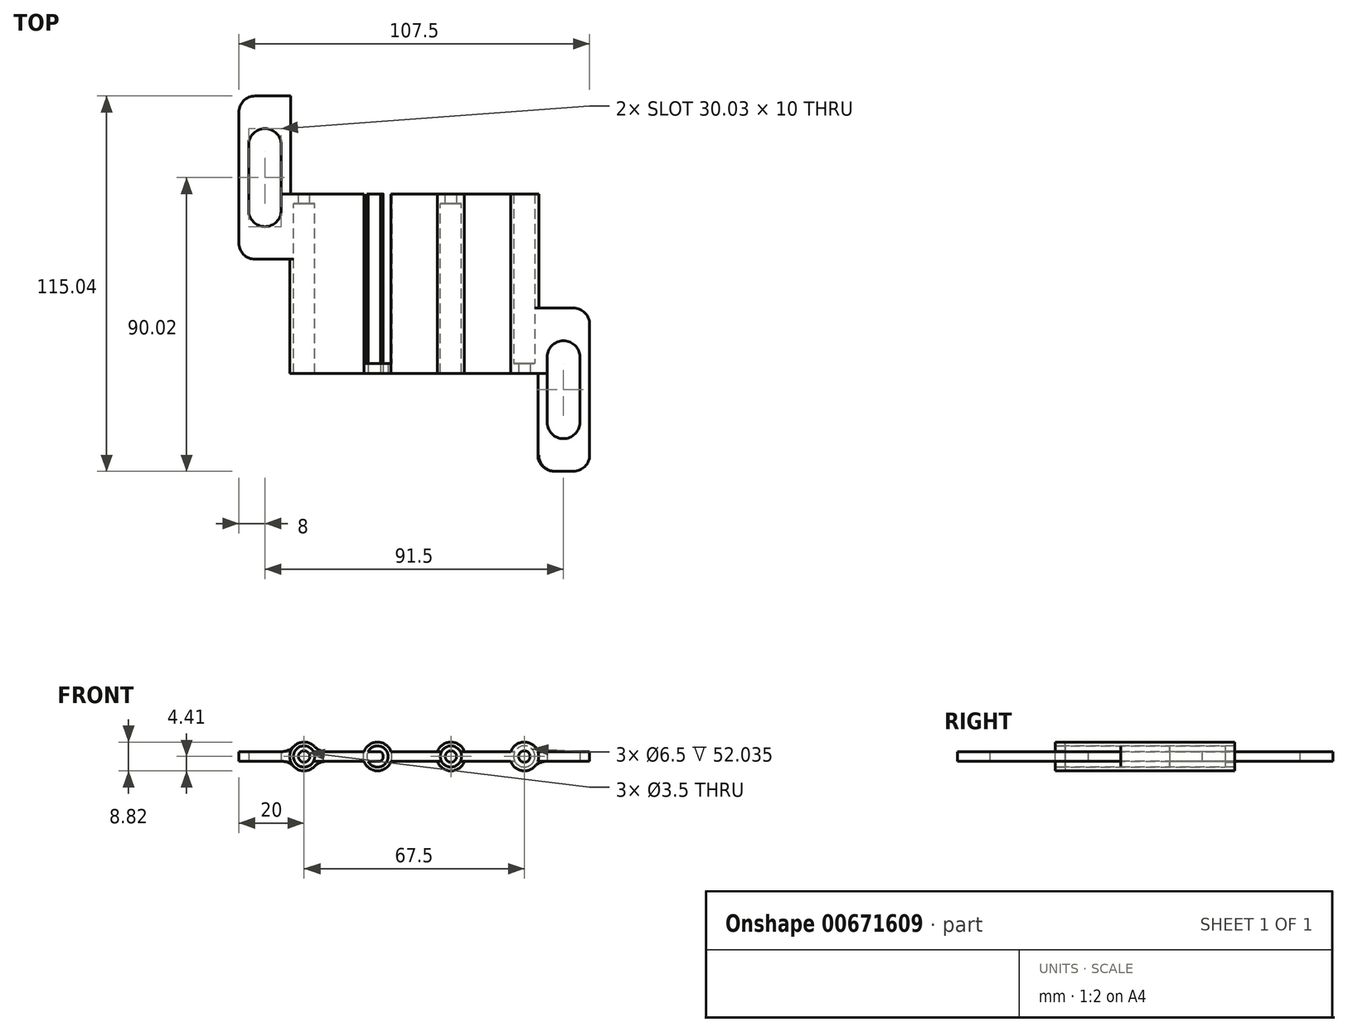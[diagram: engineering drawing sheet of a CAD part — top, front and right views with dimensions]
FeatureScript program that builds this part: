
annotation { "Feature Type Name" : "Feature", "Feature Type Description" : "" }
export const myFeature = defineFeature(function(context is Context, id is Id, definition is map)
    precondition{}
    {
        {
            var Q0;
            Q0=qCreatedBy(makeId("Top.planeOp"),FACE);
            var sketch = newSketch(context, id + "F0", { "sketchPlane" : qUnion([Q0])});
            skLineSegment(sketch, "E0.bottom", {"start": v(36.75, 27.52) * mm, "end": v(-30.75, 27.52) * mm});
            skLineSegment(sketch, "E0.top", {"start": v(36.75, -27.52) * mm, "end": v(-30.75, -27.52) * mm});
            skLineSegment(sketch, "E0.left", {"start": v(36.75, 27.52) * mm, "end": v(36.75, -27.52) * mm});
            skLineSegment(sketch, "E0.right", {"start": v(-30.75, 57.52) * mm, "end": v(-30.75, -27.52) * mm});
            skPoint(sketch, "E0.middle", {"position": v(0, 0) * mm});
            skLineSegment(sketch, "E1.left", {"start": v(36.75, 27.52) * mm, "end": v(36.75, -57.52) * mm});
            skLineSegment(sketch, "E2.0", {"start": v(56.75, -7.48) * mm, "end": v(56.75, -57.52) * mm});
            skLineSegment(sketch, "E3.0", {"start": v(-50.75, 57.52) * mm, "end": v(-50.75, 7.48) * mm});
            skLineSegment(sketch, "E4", {"start": v(36.75, -7.48) * mm, "end": v(56.75, -7.48) * mm});
            skLineSegment(sketch, "E5", {"start": v(-30.75, 7.48) * mm, "end": v(-50.75, 7.48) * mm});
            skLineSegment(sketch, "E6.0", {"start": v(-30.75, 57.52) * mm, "end": v(-50.75, 57.52) * mm});
            skLineSegment(sketch, "E7.0", {"start": v(36.75, -57.52) * mm, "end": v(56.75, -57.52) * mm});
            skLineSegment(sketch, "E8.0", {"start": v(-47.75, 47.52) * mm, "end": v(-47.75, 17.48) * mm});
            skLineSegment(sketch, "E9.0", {"start": v(-37.75, 47.52) * mm, "end": v(-37.75, 17.48) * mm});
            skLineSegment(sketch, "E10.0", {"start": v(-37.75, 47.52) * mm, "end": v(-47.75, 47.52) * mm});
            skLineSegment(sketch, "E11.0", {"start": v(-37.75, 17.48) * mm, "end": v(-47.75, 17.48) * mm});
            skLineSegment(sketch, "E12.0", {"start": v(43.75, -17.48) * mm, "end": v(53.75, -17.48) * mm});
            skLineSegment(sketch, "E13.0", {"start": v(43.75, -47.52) * mm, "end": v(53.75, -47.52) * mm});
            skLineSegment(sketch, "E14.0", {"start": v(53.75, -17.48) * mm, "end": v(53.75, -47.52) * mm});
            skLineSegment(sketch, "E15.trimOffspring", {"start": v(43.75, -17.48) * mm, "end": v(43.75, -47.52) * mm});
            skLineSegment(sketch, "E16", {"start": v(-47.75, 32.5) * mm, "end": v(23.52, 32.5) * mm, "construction": true});
            skLineSegment(sketch, "E17", {"start": v(43.75, -32.5) * mm, "end": v(9.04, -32.5) * mm, "construction": true});
            skSolve(sketch);
        }
        {
            var Q0;
            Q0=makeQuery(id+"F0.imprint","IMPRINT",FACE,{"disambiguationData":[TD([[makeQuery(id+"F0.imprint","IMPRINT",EDGE,{"derivedFrom":sQuery(id+"F0.wireOp",EDGE,"E0.bottom")}),1.0]])]});
            extrude(context, id + "F1", {"entities" : qUnion([Q0]), "depth" : 3 * mm, "offsetDistance" : 25 * mm});
        }
        {
            var Q0;
            Q0=makeQuery(id+"F1.opExtrude","SWEPT_FACE",FACE,{"disambiguationData":[OSD([sQuery(id+"F0.wireOp",EDGE,"E0.top")])]});
            var sketch = newSketch(context, id + "F2", { "sketchPlane" : qUnion([Q0])});
            skCircle(sketch, "E18", {"center": v(36.75, 1.5) * mm, "radius": 1.75 * mm});
            skCircle(sketch, "E19", {"center": v(36.75, 1.5) * mm, "radius": 3.25 * mm});
            skCircle(sketch, "E20", {"center": v(36.75, 1.5) * mm, "radius": 4.4 * mm});
            skLineSegment(sketch, "E21", {"start": v(36.75, 1.5) * mm, "end": v(36.75, 12.8) * mm, "construction": true});
            skLineSegment(sketch, "E22.0", {"start": v(-8.25, 1.5) * mm, "end": v(-8.25, 12.8) * mm, "construction": true});
            skLineSegment(sketch, "E23", {"start": v(-8.25, 12.8) * mm, "end": v(36.75, 12.8) * mm, "construction": true});
            skLineSegment(sketch, "E24", {"start": v(14.25, 12.8) * mm, "end": v(14.25, 1.5) * mm, "construction": true});
            skCircle(sketch, "E25.MirrorC", {"center": v(-8.25, 1.5) * mm, "radius": 4.4 * mm});
            skCircle(sketch, "E26.MirrorC", {"center": v(-8.25, 1.5) * mm, "radius": 3.25 * mm});
            skCircle(sketch, "E27.MirrorC", {"center": v(-8.25, 1.5) * mm, "radius": 1.75 * mm});
            skSolve(sketch);
        }
        {
            var Q0;
            Q0 = qSketchRegion(id + "F2", true);
            extrude(context, id + "F3", {"entities" : qUnion([Q0]), "operationType" : NewBodyOperationType.ADD, "oppositeDirection" : true, "depth" : 55 * mm, "offsetDistance" : 25 * mm});
        }
        {
            var Q0;
            {var subQ0=sQuery(id+"F2.wireOp",EDGE,"E18");var subQ1=sQuery(id+"F0.wireOp",EDGE,"E0.top");var subQ2=makeQuery(id+"F1.opExtrude","CAP_EDGE",EDGE,{"disambiguationData":[OSD([subQ1])],"isStart":true});var subQ3=makeQuery(id+"F2.imprint","INTERSECT",VERTEX,{"derivedFrom":[subQ2,subQ0]});Q0=makeQuery(id+"F2.imprint","IMPRINT",FACE,{"disambiguationData":[TD([[makeQuery(id+"F2.imprint","IMPRINT",EDGE,{"disambiguationData":[TD([[subQ3,-1.0]])],"derivedFrom":subQ0}),-1.0]])]});}
            var Q1;
            {var subQ0=sQuery(id+"F2.wireOp",EDGE,"E26.MirrorC");var subQ1=makeQuery(id+"F1.opExtrude","CAP_EDGE",EDGE,{"disambiguationData":[OSD([sQuery(id+"F0.wireOp",EDGE,"E0.top")])],"isStart":true});var subQ2=makeQuery(id+"F2.imprint","INTERSECT",VERTEX,{"disambiguationData":[OD(0.0)],"derivedFrom":[subQ1,subQ0]});Q1=makeQuery(id+"F2.imprint","IMPRINT",FACE,{"disambiguationData":[TD([[makeQuery(id+"F2.imprint","IMPRINT",EDGE,{"disambiguationData":[TD([[subQ2,1.0]])],"derivedFrom":subQ0}),-1.0]])]});}
            var Q2;
            {var subQ0=sQuery(id+"F2.wireOp",EDGE,"E26.MirrorC");var subQ1=makeQuery(id+"F1.opExtrude","CAP_EDGE",EDGE,{"disambiguationData":[OSD([sQuery(id+"F0.wireOp",EDGE,"E0.top")])],"isStart":false});var subQ2=makeQuery(id+"F2.imprint","INTERSECT",VERTEX,{"disambiguationData":[OD(0.0)],"derivedFrom":[subQ1,subQ0]});Q2=makeQuery(id+"F2.imprint","IMPRINT",FACE,{"disambiguationData":[TD([[makeQuery(id+"F2.imprint","IMPRINT",EDGE,{"disambiguationData":[TD([[subQ2,-1.0]])],"derivedFrom":subQ0}),-1.0]])]});}
            var Q3;
            {var subQ1=sQuery(id+"F0.wireOp",EDGE,"E0.top");var subQ6=makeQuery(id+"F1.opExtrude","SWEPT_EDGE",EDGE,{"disambiguationData":[OSD([subQ1,sQuery(id+"F0.wireOp",EDGE,"E0.left")])]});Q3=makeQuery(id+"F2.imprint","IMPRINT",FACE,{"disambiguationData":[TD([[makeQuery(id+"F2.imprint","IMPRINT",EDGE,{"derivedFrom":subQ6}),-1.0]])]});}
            var Q4;
            {var subQ0=sQuery(id+"F2.wireOp",EDGE,"E18");var subQ1=sQuery(id+"F0.wireOp",EDGE,"E0.top");var subQ2=makeQuery(id+"F1.opExtrude","CAP_EDGE",EDGE,{"disambiguationData":[OSD([subQ1])],"isStart":true});var subQ3=makeQuery(id+"F2.imprint","INTERSECT",VERTEX,{"derivedFrom":[subQ2,subQ0]});Q4=makeQuery(id+"F2.imprint","IMPRINT",FACE,{"disambiguationData":[TD([[makeQuery(id+"F2.imprint","IMPRINT",EDGE,{"disambiguationData":[TD([[subQ3,1.0]])],"derivedFrom":subQ0}),-1.0]])]});}
            var Q5;
            {var subQ0=sQuery(id+"F2.wireOp",EDGE,"E26.MirrorC");var subQ1=sQuery(id+"F0.wireOp",EDGE,"E0.top");var subQ2=makeQuery(id+"F1.opExtrude","CAP_EDGE",EDGE,{"disambiguationData":[OSD([subQ1])],"isStart":false});var subQ3=makeQuery(id+"F2.imprint","INTERSECT",VERTEX,{"disambiguationData":[OD(0.0)],"derivedFrom":[subQ2,subQ0]});Q5=makeQuery(id+"F2.imprint","IMPRINT",FACE,{"disambiguationData":[TD([[makeQuery(id+"F2.imprint","IMPRINT",EDGE,{"disambiguationData":[TD([[subQ3,1.0]])],"derivedFrom":subQ0}),-1.0]])]});}
            var Q6;
            {var subQ0=sQuery(id+"F2.wireOp",EDGE,"E27.MirrorC");var subQ1=sQuery(id+"F0.wireOp",EDGE,"E0.top");var subQ2=makeQuery(id+"F1.opExtrude","CAP_EDGE",EDGE,{"disambiguationData":[OSD([subQ1])],"isStart":false});var subQ3=makeQuery(id+"F2.imprint","INTERSECT",VERTEX,{"disambiguationData":[OD(0.0)],"derivedFrom":[subQ2,subQ0]});Q6=makeQuery(id+"F2.imprint","IMPRINT",FACE,{"disambiguationData":[TD([[makeQuery(id+"F2.imprint","IMPRINT",EDGE,{"disambiguationData":[TD([[subQ3,1.0]])],"derivedFrom":subQ0}),-1.0]])]});}
            var Q7;
            {var subQ0=sQuery(id+"F2.wireOp",EDGE,"E26.MirrorC");var subQ1=sQuery(id+"F0.wireOp",EDGE,"E0.top");var subQ2=makeQuery(id+"F1.opExtrude","CAP_EDGE",EDGE,{"disambiguationData":[OSD([subQ1])],"isStart":false});var subQ3=makeQuery(id+"F2.imprint","INTERSECT",VERTEX,{"disambiguationData":[OD(1.0)],"derivedFrom":[subQ2,subQ0]});Q7=makeQuery(id+"F2.imprint","IMPRINT",FACE,{"disambiguationData":[TD([[makeQuery(id+"F2.imprint","IMPRINT",EDGE,{"disambiguationData":[TD([[subQ3,-1.0]])],"derivedFrom":subQ0}),-1.0]])]});}
            extrude(context, id + "F4", {"entities" : qUnion([Q0, Q1, Q2, Q3, Q4, Q5, Q6, Q7]), "operationType" : NewBodyOperationType.REMOVE, "oppositeDirection" : true, "depth" : 60 * mm, "offsetDistance" : 25 * mm});
        }
        {
            var Q0;
            {var subQ0=sQuery(id+"F2.wireOp",EDGE,"E26.MirrorC");var subQ1=makeQuery(id+"F1.opExtrude","CAP_EDGE",EDGE,{"disambiguationData":[OSD([sQuery(id+"F0.wireOp",EDGE,"E0.top")])],"isStart":false});var subQ2=makeQuery(id+"F2.imprint","INTERSECT",VERTEX,{"disambiguationData":[OD(0.0)],"derivedFrom":[subQ1,subQ0]});Q0=makeQuery(id+"F2.imprint","IMPRINT",FACE,{"disambiguationData":[TD([[makeQuery(id+"F2.imprint","IMPRINT",EDGE,{"disambiguationData":[TD([[subQ2,-1.0]])],"derivedFrom":subQ0}),-1.0]])]});}
            var Q1;
            {var subQ0=sQuery(id+"F2.wireOp",EDGE,"E26.MirrorC");var subQ1=sQuery(id+"F0.wireOp",EDGE,"E0.top");var subQ2=makeQuery(id+"F1.opExtrude","CAP_EDGE",EDGE,{"disambiguationData":[OSD([subQ1])],"isStart":false});var subQ3=makeQuery(id+"F2.imprint","INTERSECT",VERTEX,{"disambiguationData":[OD(0.0)],"derivedFrom":[subQ2,subQ0]});Q1=makeQuery(id+"F2.imprint","IMPRINT",FACE,{"disambiguationData":[TD([[makeQuery(id+"F2.imprint","IMPRINT",EDGE,{"disambiguationData":[TD([[subQ3,1.0]])],"derivedFrom":subQ0}),-1.0]])]});}
            var Q2;
            {var subQ0=sQuery(id+"F2.wireOp",EDGE,"E26.MirrorC");var subQ1=makeQuery(id+"F1.opExtrude","CAP_EDGE",EDGE,{"disambiguationData":[OSD([sQuery(id+"F0.wireOp",EDGE,"E0.top")])],"isStart":true});var subQ2=makeQuery(id+"F2.imprint","INTERSECT",VERTEX,{"disambiguationData":[OD(0.0)],"derivedFrom":[subQ1,subQ0]});Q2=makeQuery(id+"F2.imprint","IMPRINT",FACE,{"disambiguationData":[TD([[makeQuery(id+"F2.imprint","IMPRINT",EDGE,{"disambiguationData":[TD([[subQ2,1.0]])],"derivedFrom":subQ0}),-1.0]])]});}
            var Q3;
            {var subQ0=sQuery(id+"F2.wireOp",EDGE,"E26.MirrorC");var subQ1=sQuery(id+"F0.wireOp",EDGE,"E0.top");var subQ2=makeQuery(id+"F1.opExtrude","CAP_EDGE",EDGE,{"disambiguationData":[OSD([subQ1])],"isStart":false});var subQ3=makeQuery(id+"F2.imprint","INTERSECT",VERTEX,{"disambiguationData":[OD(1.0)],"derivedFrom":[subQ2,subQ0]});Q3=makeQuery(id+"F2.imprint","IMPRINT",FACE,{"disambiguationData":[TD([[makeQuery(id+"F2.imprint","IMPRINT",EDGE,{"disambiguationData":[TD([[subQ3,-1.0]])],"derivedFrom":subQ0}),-1.0]])]});}
            var Q4;
            {var subQ0=sQuery(id+"F2.wireOp",EDGE,"E18");var subQ1=sQuery(id+"F0.wireOp",EDGE,"E0.top");var subQ2=makeQuery(id+"F1.opExtrude","CAP_EDGE",EDGE,{"disambiguationData":[OSD([subQ1])],"isStart":true});var subQ3=makeQuery(id+"F2.imprint","INTERSECT",VERTEX,{"derivedFrom":[subQ2,subQ0]});Q4=makeQuery(id+"F2.imprint","IMPRINT",FACE,{"disambiguationData":[TD([[makeQuery(id+"F2.imprint","IMPRINT",EDGE,{"disambiguationData":[TD([[subQ3,1.0]])],"derivedFrom":subQ0}),-1.0]])]});}
            var Q5;
            {var subQ0=sQuery(id+"F2.wireOp",EDGE,"E18");var subQ1=sQuery(id+"F0.wireOp",EDGE,"E0.top");var subQ2=makeQuery(id+"F1.opExtrude","CAP_EDGE",EDGE,{"disambiguationData":[OSD([subQ1])],"isStart":true});var subQ3=makeQuery(id+"F2.imprint","INTERSECT",VERTEX,{"derivedFrom":[subQ2,subQ0]});Q5=makeQuery(id+"F2.imprint","IMPRINT",FACE,{"disambiguationData":[TD([[makeQuery(id+"F2.imprint","IMPRINT",EDGE,{"disambiguationData":[TD([[subQ3,-1.0]])],"derivedFrom":subQ0}),-1.0]])]});}
            extrude(context, id + "F5", {"entities" : qUnion([Q0, Q1, Q2, Q3, Q4, Q5]), "operationType" : NewBodyOperationType.ADD, "oppositeDirection" : true, "depth" : 3 * mm, "offsetDistance" : 25 * mm});
        }
        {
            var Q0;
            {var subQ1=sQuery(id+"F2.wireOp",EDGE,"E19");var subQ5=sQuery(id+"F0.wireOp",EDGE,"E0.bottom");Q0=makeQuery(id+"F4.boolean.opBoolean","SPLIT",FACE,{"disambiguationData":[TD([makeQuery(id+"F3.opExtrude","SWEPT_FACE",FACE,{"disambiguationData":[OSD([subQ1])]})])],"derivedFrom":makeQuery(id+"F1.opExtrude","SWEPT_FACE",FACE,{"disambiguationData":[OSD([subQ5])]})});}
            var sketch = newSketch(context, id + "F6", { "sketchPlane" : qUnion([Q0])});
            skLineSegment(sketch, "E28", {"start": v(-14.25, 3) * mm, "end": v(-14.25, 0) * mm, "construction": true});
            skCircle(sketch, "E29", {"center": v(-14.25, 1.5) * mm, "radius": 1.75 * mm});
            skCircle(sketch, "E30", {"center": v(-14.25, 1.5) * mm, "radius": 3.25 * mm});
            skCircle(sketch, "E31", {"center": v(-14.25, 1.5) * mm, "radius": 4.4 * mm});
            skCircle(sketch, "E32.1.0.0", {"center": v(30.75, 1.5) * mm, "radius": 4.4 * mm});
            skCircle(sketch, "E32.1.0.1", {"center": v(30.75, 1.5) * mm, "radius": 3.25 * mm});
            skCircle(sketch, "E32.1.0.2", {"center": v(30.75, 1.5) * mm, "radius": 1.75 * mm});
            skLineSegment(sketch, "E32.direction1", {"start": v(-14.25, 1.5) * mm, "end": v(30.75, 1.5) * mm, "construction": true});
            skSolve(sketch);
        }
        {
            var Q0;
            Q0=makeQuery(id+"F0.imprint","IMPRINT",FACE,{"disambiguationData":[TD([[makeQuery(id+"F0.imprint","IMPRINT",EDGE,{"derivedFrom":sQuery(id+"F0.wireOp",EDGE,"E0.right")}),-1.0]])]});
            var Q1;
            {var subQ1=sQuery(id+"F0.wireOp",EDGE,"E1.left");Q1=makeQuery(id+"F0.imprint","IMPRINT",FACE,{"disambiguationData":[TD([[makeQuery(id+"F0.imprint","IMPRINT",EDGE,{"derivedFrom":subQ1}),1.0]])]});}
            extrude(context, id + "F7", {"entities" : qUnion([Q0, Q1]), "operationType" : NewBodyOperationType.ADD, "depth" : 3 * mm, "offsetDistance" : 25 * mm});
        }
        {
            var Q0;
            {var subQ0=sQuery(id+"F6.wireOp",EDGE,"E30");var subQ1=sQuery(id+"F2.wireOp",EDGE,"E19");var subQ2=sQuery(id+"F0.wireOp",EDGE,"E0.bottom");var subQ4=makeQuery(id+"F4.boolean.opBoolean","SPLIT",EDGE,{"disambiguationData":[TD([makeQuery(id+"F3.opExtrude","SWEPT_FACE",FACE,{"disambiguationData":[OSD([subQ1])]})])],"derivedFrom":makeQuery(id+"F1.opExtrude","CAP_EDGE",EDGE,{"disambiguationData":[OSD([subQ2])],"isStart":false})});var subQ5=makeQuery(id+"F6.imprint","INTERSECT",VERTEX,{"disambiguationData":[OD(0.0)],"derivedFrom":[subQ4,subQ0]});Q0=makeQuery(id+"F6.imprint","IMPRINT",FACE,{"disambiguationData":[TD([[makeQuery(id+"F6.imprint","IMPRINT",EDGE,{"disambiguationData":[TD([[subQ5,1.0]])],"derivedFrom":subQ0}),-1.0]])]});}
            var Q1;
            {var subQ0=sQuery(id+"F6.wireOp",EDGE,"E30");var subQ1=sQuery(id+"F2.wireOp",EDGE,"E19");var subQ2=sQuery(id+"F0.wireOp",EDGE,"E0.bottom");var subQ4=makeQuery(id+"F4.boolean.opBoolean","SPLIT",EDGE,{"disambiguationData":[TD([makeQuery(id+"F3.opExtrude","SWEPT_FACE",FACE,{"disambiguationData":[OSD([subQ1])]})])],"derivedFrom":makeQuery(id+"F1.opExtrude","CAP_EDGE",EDGE,{"disambiguationData":[OSD([subQ2])],"isStart":true})});var subQ5=makeQuery(id+"F6.imprint","INTERSECT",VERTEX,{"disambiguationData":[OD(0.0)],"derivedFrom":[subQ4,subQ0]});Q1=makeQuery(id+"F6.imprint","IMPRINT",FACE,{"disambiguationData":[TD([[makeQuery(id+"F6.imprint","IMPRINT",EDGE,{"disambiguationData":[TD([[subQ5,-1.0]])],"derivedFrom":subQ0}),-1.0]])]});}
            var Q2;
            Q2=makeQuery(id+"F6.imprint","IMPRINT",FACE,{"disambiguationData":[TD([[makeQuery(id+"F6.imprint","IMPRINT",EDGE,{"derivedFrom":sQuery(id+"F6.wireOp",EDGE,"E32.1.0.0")}),1.0]])]});
            extrude(context, id + "F8", {"entities" : qUnion([Q0, Q1, Q2]), "operationType" : NewBodyOperationType.ADD, "oppositeDirection" : true, "depth" : 55 * mm, "offsetDistance" : 25 * mm});
        }
        {
            var Q0;
            {var subQ0=sQuery(id+"F6.wireOp",EDGE,"E29");var subQ1=sQuery(id+"F2.wireOp",EDGE,"E19");var subQ2=makeQuery(id+"F3.opExtrude","SWEPT_FACE",FACE,{"disambiguationData":[OSD([subQ1])]});var subQ6=sQuery(id+"F0.wireOp",EDGE,"E0.bottom");var subQ12=makeQuery(id+"F4.boolean.opBoolean","SPLIT",EDGE,{"disambiguationData":[TD([subQ2])],"derivedFrom":makeQuery(id+"F1.opExtrude","CAP_EDGE",EDGE,{"disambiguationData":[OSD([subQ6])],"isStart":true})});var subQ13=makeQuery(id+"F6.imprint","INTERSECT",VERTEX,{"disambiguationData":[OD(0.0)],"derivedFrom":[subQ12,subQ0]});Q0=makeQuery(id+"F6.imprint","IMPRINT",FACE,{"disambiguationData":[TD([[makeQuery(id+"F6.imprint","IMPRINT",EDGE,{"disambiguationData":[TD([[subQ13,1.0]])],"derivedFrom":subQ0}),-1.0]])]});}
            var Q1;
            {var subQ0=sQuery(id+"F6.wireOp",EDGE,"E29");var subQ1=sQuery(id+"F2.wireOp",EDGE,"E19");var subQ2=makeQuery(id+"F3.opExtrude","SWEPT_FACE",FACE,{"disambiguationData":[OSD([subQ1])]});var subQ6=sQuery(id+"F0.wireOp",EDGE,"E0.bottom");var subQ12=makeQuery(id+"F4.boolean.opBoolean","SPLIT",EDGE,{"disambiguationData":[TD([subQ2])],"derivedFrom":makeQuery(id+"F1.opExtrude","CAP_EDGE",EDGE,{"disambiguationData":[OSD([subQ6])],"isStart":true})});var subQ13=makeQuery(id+"F6.imprint","INTERSECT",VERTEX,{"disambiguationData":[OD(0.0)],"derivedFrom":[subQ12,subQ0]});Q1=makeQuery(id+"F6.imprint","IMPRINT",FACE,{"disambiguationData":[TD([[makeQuery(id+"F6.imprint","IMPRINT",EDGE,{"disambiguationData":[TD([[subQ13,1.0]])],"derivedFrom":subQ0}),1.0]])]});}
            var Q2;
            {var subQ0=sQuery(id+"F6.wireOp",EDGE,"E29");var subQ1=sQuery(id+"F2.wireOp",EDGE,"E19");var subQ2=makeQuery(id+"F3.opExtrude","SWEPT_FACE",FACE,{"disambiguationData":[OSD([subQ1])]});var subQ6=sQuery(id+"F0.wireOp",EDGE,"E0.bottom");var subQ12=makeQuery(id+"F4.boolean.opBoolean","SPLIT",EDGE,{"disambiguationData":[TD([subQ2])],"derivedFrom":makeQuery(id+"F1.opExtrude","CAP_EDGE",EDGE,{"disambiguationData":[OSD([subQ6])],"isStart":true})});var subQ13=makeQuery(id+"F6.imprint","INTERSECT",VERTEX,{"disambiguationData":[OD(1.0)],"derivedFrom":[subQ12,subQ0]});Q2=makeQuery(id+"F6.imprint","IMPRINT",FACE,{"disambiguationData":[TD([[makeQuery(id+"F6.imprint","IMPRINT",EDGE,{"disambiguationData":[TD([[subQ13,-1.0]])],"derivedFrom":subQ0}),-1.0]])]});}
            var Q3;
            Q3=makeQuery(id+"F6.imprint","IMPRINT",FACE,{"disambiguationData":[TD([[makeQuery(id+"F6.imprint","IMPRINT",EDGE,{"derivedFrom":sQuery(id+"F6.wireOp",EDGE,"E32.1.0.2")}),1.0]])]});
            var Q4;
            Q4=makeQuery(id+"F6.imprint","IMPRINT",FACE,{"disambiguationData":[TD([[makeQuery(id+"F6.imprint","IMPRINT",EDGE,{"derivedFrom":sQuery(id+"F6.wireOp",EDGE,"E32.1.0.1")}),1.0]])]});
            extrude(context, id + "F9", {"entities" : qUnion([Q0, Q1, Q2, Q3, Q4]), "operationType" : NewBodyOperationType.REMOVE, "oppositeDirection" : true, "depth" : 60 * mm, "offsetDistance" : 25 * mm});
        }
        {
            var Q0;
            {var subQ0=sQuery(id+"F6.wireOp",EDGE,"E29");var subQ1=sQuery(id+"F2.wireOp",EDGE,"E19");var subQ2=sQuery(id+"F0.wireOp",EDGE,"E0.bottom");var subQ4=makeQuery(id+"F4.boolean.opBoolean","SPLIT",EDGE,{"disambiguationData":[TD([makeQuery(id+"F3.opExtrude","SWEPT_FACE",FACE,{"disambiguationData":[OSD([subQ1])]})])],"derivedFrom":makeQuery(id+"F1.opExtrude","CAP_EDGE",EDGE,{"disambiguationData":[OSD([subQ2])],"isStart":false})});var subQ5=makeQuery(id+"F6.imprint","INTERSECT",VERTEX,{"disambiguationData":[OD(0.0)],"derivedFrom":[subQ4,subQ0]});Q0=makeQuery(id+"F6.imprint","IMPRINT",FACE,{"disambiguationData":[TD([[makeQuery(id+"F6.imprint","IMPRINT",EDGE,{"disambiguationData":[TD([[subQ5,1.0]])],"derivedFrom":subQ0}),-1.0]])]});}
            var Q1;
            {var subQ0=sQuery(id+"F6.wireOp",EDGE,"E29");var subQ1=sQuery(id+"F2.wireOp",EDGE,"E19");var subQ2=makeQuery(id+"F3.opExtrude","SWEPT_FACE",FACE,{"disambiguationData":[OSD([subQ1])]});var subQ6=sQuery(id+"F0.wireOp",EDGE,"E0.bottom");var subQ12=makeQuery(id+"F4.boolean.opBoolean","SPLIT",EDGE,{"disambiguationData":[TD([subQ2])],"derivedFrom":makeQuery(id+"F1.opExtrude","CAP_EDGE",EDGE,{"disambiguationData":[OSD([subQ6])],"isStart":true})});var subQ13=makeQuery(id+"F6.imprint","INTERSECT",VERTEX,{"disambiguationData":[OD(1.0)],"derivedFrom":[subQ12,subQ0]});Q1=makeQuery(id+"F6.imprint","IMPRINT",FACE,{"disambiguationData":[TD([[makeQuery(id+"F6.imprint","IMPRINT",EDGE,{"disambiguationData":[TD([[subQ13,-1.0]])],"derivedFrom":subQ0}),-1.0]])]});}
            var Q2;
            {var subQ0=sQuery(id+"F6.wireOp",EDGE,"E29");var subQ1=sQuery(id+"F2.wireOp",EDGE,"E19");var subQ2=sQuery(id+"F0.wireOp",EDGE,"E0.bottom");var subQ4=makeQuery(id+"F4.boolean.opBoolean","SPLIT",EDGE,{"disambiguationData":[TD([makeQuery(id+"F3.opExtrude","SWEPT_FACE",FACE,{"disambiguationData":[OSD([subQ1])]})])],"derivedFrom":makeQuery(id+"F1.opExtrude","CAP_EDGE",EDGE,{"disambiguationData":[OSD([subQ2])],"isStart":true})});var subQ5=makeQuery(id+"F6.imprint","INTERSECT",VERTEX,{"disambiguationData":[OD(0.0)],"derivedFrom":[subQ4,subQ0]});Q2=makeQuery(id+"F6.imprint","IMPRINT",FACE,{"disambiguationData":[TD([[makeQuery(id+"F6.imprint","IMPRINT",EDGE,{"disambiguationData":[TD([[subQ5,-1.0]])],"derivedFrom":subQ0}),-1.0]])]});}
            var Q3;
            {var subQ0=sQuery(id+"F6.wireOp",EDGE,"E29");var subQ1=sQuery(id+"F2.wireOp",EDGE,"E19");var subQ2=makeQuery(id+"F3.opExtrude","SWEPT_FACE",FACE,{"disambiguationData":[OSD([subQ1])]});var subQ6=sQuery(id+"F0.wireOp",EDGE,"E0.bottom");var subQ12=makeQuery(id+"F4.boolean.opBoolean","SPLIT",EDGE,{"disambiguationData":[TD([subQ2])],"derivedFrom":makeQuery(id+"F1.opExtrude","CAP_EDGE",EDGE,{"disambiguationData":[OSD([subQ6])],"isStart":true})});var subQ13=makeQuery(id+"F6.imprint","INTERSECT",VERTEX,{"disambiguationData":[OD(0.0)],"derivedFrom":[subQ12,subQ0]});Q3=makeQuery(id+"F6.imprint","IMPRINT",FACE,{"disambiguationData":[TD([[makeQuery(id+"F6.imprint","IMPRINT",EDGE,{"disambiguationData":[TD([[subQ13,1.0]])],"derivedFrom":subQ0}),-1.0]])]});}
            var Q4;
            Q4=makeQuery(id+"F6.imprint","IMPRINT",FACE,{"disambiguationData":[TD([[makeQuery(id+"F6.imprint","IMPRINT",EDGE,{"derivedFrom":sQuery(id+"F6.wireOp",EDGE,"E32.1.0.1")}),1.0]])]});
            extrude(context, id + "F10", {"entities" : qUnion([Q0, Q1, Q2, Q3, Q4]), "operationType" : NewBodyOperationType.ADD, "oppositeDirection" : true, "depth" : 3 * mm, "offsetDistance" : 25 * mm});
        }
        {
            var Q0;
            {var subQ0=sQuery(id+"F2.wireOp",EDGE,"E18");var subQ1=sQuery(id+"F0.wireOp",EDGE,"E0.top");var subQ2=makeQuery(id+"F1.opExtrude","CAP_EDGE",EDGE,{"disambiguationData":[OSD([subQ1])],"isStart":true});var subQ3=makeQuery(id+"F2.imprint","INTERSECT",VERTEX,{"derivedFrom":[subQ2,subQ0]});Q0=makeQuery(id+"F2.imprint","IMPRINT",FACE,{"disambiguationData":[TD([[makeQuery(id+"F2.imprint","IMPRINT",EDGE,{"disambiguationData":[TD([[subQ3,-1.0]])],"derivedFrom":subQ0}),-1.0]])]});}
            var Q1;
            {var subQ1=sQuery(id+"F0.wireOp",EDGE,"E0.top");var subQ6=makeQuery(id+"F1.opExtrude","SWEPT_EDGE",EDGE,{"disambiguationData":[OSD([subQ1,sQuery(id+"F0.wireOp",EDGE,"E0.left"),sQuery(id+"F0.wireOp",EDGE,"SqTT4nLf-HDbF-SFdv-T9V0-0vRYkoL7qoO4")])]});Q1=makeQuery(id+"F2.imprint","IMPRINT",FACE,{"disambiguationData":[TD([[makeQuery(id+"F2.imprint","IMPRINT",EDGE,{"derivedFrom":subQ6}),1.0]])]});}
            extrude(context, id + "F11", {"entities" : qUnion([Q0, Q1]), "operationType" : NewBodyOperationType.REMOVE, "oppositeDirection" : true, "depth" : 60 * mm, "offsetDistance" : 25 * mm});
        }
        {
            var Q0;
            {var subQ0=sQuery(id+"F2.wireOp",EDGE,"E18");var subQ1=sQuery(id+"F0.wireOp",EDGE,"E0.top");var subQ2=makeQuery(id+"F1.opExtrude","CAP_EDGE",EDGE,{"disambiguationData":[OSD([subQ1])],"isStart":true});var subQ3=makeQuery(id+"F2.imprint","INTERSECT",VERTEX,{"derivedFrom":[subQ2,subQ0]});Q0=makeQuery(id+"F2.imprint","IMPRINT",FACE,{"disambiguationData":[TD([[makeQuery(id+"F2.imprint","IMPRINT",EDGE,{"disambiguationData":[TD([[subQ3,-1.0]])],"derivedFrom":subQ0}),-1.0]])]});}
            extrude(context, id + "F12", {"entities" : qUnion([Q0]), "operationType" : NewBodyOperationType.ADD, "oppositeDirection" : true, "depth" : 3 * mm, "offsetDistance" : 25 * mm});
        }
        {
            var Q0;
            {var subQ0=sQuery(id+"F2.wireOp",EDGE,"E18");var subQ1=sQuery(id+"F0.wireOp",EDGE,"E0.top");var subQ2=makeQuery(id+"F1.opExtrude","CAP_EDGE",EDGE,{"disambiguationData":[OSD([subQ1])],"isStart":true});var subQ3=makeQuery(id+"F2.imprint","INTERSECT",VERTEX,{"derivedFrom":[subQ2,subQ0]});Q0=makeQuery(id+"F2.imprint","IMPRINT",FACE,{"disambiguationData":[TD([[makeQuery(id+"F2.imprint","IMPRINT",EDGE,{"disambiguationData":[TD([[subQ3,-1.0]])],"derivedFrom":subQ0}),-1.0]])]});}
            var Q1;
            Q1=makeQuery(id+"F7.opExtrude","SWEPT_FACE",FACE,{"disambiguationData":[OSD([sQuery(id+"F0.wireOp",EDGE,"E7.0")])]});
            var Q2;
            {var subQ1=sQuery(id+"F0.wireOp",EDGE,"E0.top");var subQ6=makeQuery(id+"F1.opExtrude","SWEPT_EDGE",EDGE,{"disambiguationData":[OSD([subQ1,sQuery(id+"F0.wireOp",EDGE,"E0.left"),sQuery(id+"F0.wireOp",EDGE,"E1.left")])]});Q2=makeQuery(id+"F2.imprint","IMPRINT",FACE,{"disambiguationData":[TD([[makeQuery(id+"F2.imprint","IMPRINT",EDGE,{"derivedFrom":subQ6}),1.0]])]});}
            var Q3;
            {var subQ0=sQuery(id+"F2.wireOp",EDGE,"E19");var subQ1=sQuery(id+"F0.wireOp",EDGE,"E0.top");var subQ2=makeQuery(id+"F1.opExtrude","CAP_EDGE",EDGE,{"disambiguationData":[OSD([subQ1])],"isStart":true});var subQ3=makeQuery(id+"F2.imprint","INTERSECT",VERTEX,{"derivedFrom":[subQ2,subQ0]});Q3=makeQuery(id+"F2.imprint","IMPRINT",FACE,{"disambiguationData":[TD([[makeQuery(id+"F2.imprint","IMPRINT",EDGE,{"disambiguationData":[TD([[subQ3,-1.0]])],"derivedFrom":subQ0}),-1.0]])]});}
            extrude(context, id + "F13", {"entities" : qUnion([Q0, Q1, Q2, Q3]), "operationType" : NewBodyOperationType.REMOVE, "depth" : 30 * mm, "offsetDistance" : 25 * mm});
        }
        {
            var Q0;
            Q0=makeQuery(id+"F6.imprint","IMPRINT",FACE,{"disambiguationData":[TD([[makeQuery(id+"F6.imprint","IMPRINT",EDGE,{"derivedFrom":sQuery(id+"F6.wireOp",EDGE,"E32.1.0.0")}),1.0]])]});
            var Q1;
            Q1=makeQuery(id+"F6.imprint","IMPRINT",FACE,{"disambiguationData":[TD([[makeQuery(id+"F6.imprint","IMPRINT",EDGE,{"derivedFrom":sQuery(id+"F6.wireOp",EDGE,"E32.1.0.1")}),1.0]])]});
            var Q2;
            Q2=makeQuery(id+"F6.imprint","IMPRINT",FACE,{"disambiguationData":[TD([[makeQuery(id+"F6.imprint","IMPRINT",EDGE,{"derivedFrom":sQuery(id+"F6.wireOp",EDGE,"E32.1.0.2")}),1.0]])]});
            extrude(context, id + "F14", {"entities" : qUnion([Q0, Q1, Q2]), "operationType" : NewBodyOperationType.REMOVE, "depth" : 30 * mm, "offsetDistance" : 25 * mm});
        }
        {
            var Q0;
            {var subQ0=sQuery(id+"F0.wireOp",EDGE,"E0.right");var subQ2=sQuery(id+"F0.wireOp",EDGE,"E0.top");var subQ4=sQuery(id+"F0.wireOp",EDGE,"E0.bottom");Q0=makeQuery(id+"F8.boolean.opBoolean","INTERSECT",EDGE,{"disambiguationData":[OD(1.0)],"derivedFrom":[makeQuery(id+"F7.boolean.opBoolean","MERGE",FACE,{"derivedFrom":[makeQuery(id+"F4.boolean.opBoolean","SPLIT",FACE,{"disambiguationData":[TD([makeQuery(id+"F1.opExtrude","SWEPT_FACE",FACE,{"disambiguationData":[OSD([subQ0])]})])],"derivedFrom":makeQuery(id+"F1.opExtrude","CAP_FACE",FACE,{"disambiguationData":[OSD([subQ4,subQ2,sQuery(id+"F0.wireOp",EDGE,"E0.left"),subQ0])],"isStart":false})}),makeQuery(id+"F7.opExtrude","CAP_FACE",FACE,{"disambiguationData":[OSD([subQ0,sQuery(id+"F0.wireOp",EDGE,"E3.0"),sQuery(id+"F0.wireOp",EDGE,"E5"),sQuery(id+"F0.wireOp",EDGE,"E6.0")])],"isStart":false})]}),makeQuery(id+"F8.opExtrude","SWEPT_FACE",FACE,{"disambiguationData":[OSD([sQuery(id+"F6.wireOp",EDGE,"E32.1.0.0")])]})]});}
            var Q1;
            {var subQ0=sQuery(id+"F0.wireOp",EDGE,"E0.right");var subQ2=sQuery(id+"F0.wireOp",EDGE,"E0.top");var subQ4=sQuery(id+"F0.wireOp",EDGE,"E0.bottom");Q1=makeQuery(id+"F8.boolean.opBoolean","INTERSECT",EDGE,{"disambiguationData":[OD(1.0)],"derivedFrom":[makeQuery(id+"F7.boolean.opBoolean","MERGE",FACE,{"derivedFrom":[makeQuery(id+"F4.boolean.opBoolean","SPLIT",FACE,{"disambiguationData":[TD([makeQuery(id+"F1.opExtrude","SWEPT_FACE",FACE,{"disambiguationData":[OSD([subQ0])]})])],"derivedFrom":makeQuery(id+"F1.opExtrude","CAP_FACE",FACE,{"disambiguationData":[OSD([subQ4,subQ2,sQuery(id+"F0.wireOp",EDGE,"E0.left"),subQ0])],"isStart":true})}),makeQuery(id+"F7.opExtrude","CAP_FACE",FACE,{"disambiguationData":[OSD([subQ0,sQuery(id+"F0.wireOp",EDGE,"E3.0"),sQuery(id+"F0.wireOp",EDGE,"E5"),sQuery(id+"F0.wireOp",EDGE,"E6.0")])],"isStart":true})]}),makeQuery(id+"F8.opExtrude","SWEPT_FACE",FACE,{"disambiguationData":[OSD([sQuery(id+"F6.wireOp",EDGE,"E32.1.0.0")])]})]});}
            var Q2;
            Q2=makeQuery(id+"F7.boolean.opBoolean","INTERSECT",EDGE,{"derivedFrom":[makeQuery(id+"F3.opExtrude","SWEPT_FACE",FACE,{"disambiguationData":[OSD([sQuery(id+"F2.wireOp",EDGE,"E20")])]}),makeQuery(id+"F7.opExtrude","CAP_FACE",FACE,{"disambiguationData":[OSD([sQuery(id+"F0.wireOp",EDGE,"E0.left"),sQuery(id+"F0.wireOp",EDGE,"E1.left"),sQuery(id+"F0.wireOp",EDGE,"E2.0"),sQuery(id+"F0.wireOp",EDGE,"E4"),sQuery(id+"F0.wireOp",EDGE,"E7.0")])],"isStart":true})]});
            var Q3;
            Q3=makeQuery(id+"F7.boolean.opBoolean","INTERSECT",EDGE,{"derivedFrom":[makeQuery(id+"F3.opExtrude","SWEPT_FACE",FACE,{"disambiguationData":[OSD([sQuery(id+"F2.wireOp",EDGE,"E20")])]}),makeQuery(id+"F7.opExtrude","CAP_FACE",FACE,{"disambiguationData":[OSD([sQuery(id+"F0.wireOp",EDGE,"E0.left"),sQuery(id+"F0.wireOp",EDGE,"E1.left"),sQuery(id+"F0.wireOp",EDGE,"E2.0"),sQuery(id+"F0.wireOp",EDGE,"E4"),sQuery(id+"F0.wireOp",EDGE,"E7.0")])],"isStart":false})]});
            fillet(context, id + "F15", {"entities" : qUnion([Q0, Q1, Q2, Q3]), "tangentPropagation" : true, "radius" : 5 * mm, "defaultsChanged" : false, "vertexSettings" : [], "allowEdgeOverflow" : false});
        }
        {
            var Q0;
            Q0=makeQuery(id+"F7.opExtrude","SWEPT_EDGE",EDGE,{"disambiguationData":[OSD([sQuery(id+"F0.wireOp",EDGE,"E12.0"),sQuery(id+"F0.wireOp",EDGE,"E15.trimOffspring")])]});
            var Q1;
            Q1=makeQuery(id+"F7.opExtrude","SWEPT_EDGE",EDGE,{"disambiguationData":[OSD([sQuery(id+"F0.wireOp",EDGE,"E12.0"),sQuery(id+"F0.wireOp",EDGE,"E14.0")])]});
            var Q2;
            Q2=makeQuery(id+"F7.opExtrude","SWEPT_EDGE",EDGE,{"disambiguationData":[OSD([sQuery(id+"F0.wireOp",EDGE,"E13.0"),sQuery(id+"F0.wireOp",EDGE,"E15.trimOffspring")])]});
            var Q3;
            Q3=makeQuery(id+"F7.opExtrude","SWEPT_EDGE",EDGE,{"disambiguationData":[OSD([sQuery(id+"F0.wireOp",EDGE,"E13.0"),sQuery(id+"F0.wireOp",EDGE,"E14.0")])]});
            var Q4;
            Q4=makeQuery(id+"F7.opExtrude","SWEPT_EDGE",EDGE,{"disambiguationData":[OSD([sQuery(id+"F0.wireOp",EDGE,"E9.0"),sQuery(id+"F0.wireOp",EDGE,"E11.0")])]});
            var Q5;
            Q5=makeQuery(id+"F7.opExtrude","SWEPT_EDGE",EDGE,{"disambiguationData":[OSD([sQuery(id+"F0.wireOp",EDGE,"E8.0"),sQuery(id+"F0.wireOp",EDGE,"E11.0")])]});
            var Q6;
            Q6=makeQuery(id+"F7.opExtrude","SWEPT_EDGE",EDGE,{"disambiguationData":[OSD([sQuery(id+"F0.wireOp",EDGE,"E8.0"),sQuery(id+"F0.wireOp",EDGE,"E10.0")])]});
            var Q7;
            Q7=makeQuery(id+"F7.opExtrude","SWEPT_EDGE",EDGE,{"disambiguationData":[OSD([sQuery(id+"F0.wireOp",EDGE,"E9.0"),sQuery(id+"F0.wireOp",EDGE,"E10.0")])]});
            var Q8;
            Q8=makeQuery(id+"F7.opExtrude","SWEPT_EDGE",EDGE,{"disambiguationData":[OSD([sQuery(id+"F0.wireOp",EDGE,"E3.0"),sQuery(id+"F0.wireOp",EDGE,"E5")])]});
            var Q9;
            Q9=makeQuery(id+"F7.opExtrude","SWEPT_EDGE",EDGE,{"disambiguationData":[OSD([sQuery(id+"F0.wireOp",EDGE,"E3.0"),sQuery(id+"F0.wireOp",EDGE,"E6.0")])]});
            var Q10;
            Q10=makeQuery(id+"F14.boolean.opBoolean","COPY",EDGE,{"derivedFrom":makeQuery(id+"F14.opExtrude","CAP_EDGE",EDGE,{"disambiguationData":[OSD([sQuery(id+"F6.wireOp",EDGE,"E32.1.0.0")])],"isStart":false})});
            var Q11;
            Q11=makeQuery(id+"F7.opExtrude","SWEPT_EDGE",EDGE,{"disambiguationData":[OSD([sQuery(id+"F0.wireOp",EDGE,"E2.0"),sQuery(id+"F0.wireOp",EDGE,"E4")])]});
            var Q12;
            Q12=makeQuery(id+"F7.opExtrude","SWEPT_EDGE",EDGE,{"disambiguationData":[OSD([sQuery(id+"F0.wireOp",EDGE,"E2.0"),sQuery(id+"F0.wireOp",EDGE,"E7.0")])]});
            var Q13;
            {var subQ0=sQuery(id+"F0.wireOp",EDGE,"E7.0");Q13=makeQuery(id+"F13.boolean.opBoolean","INTERSECT",EDGE,{"derivedFrom":[makeQuery(id+"F7.opExtrude","SWEPT_FACE",FACE,{"disambiguationData":[OSD([subQ0])]}),makeQuery(id+"F13.opExtrude","CAP_FACE",FACE,{"disambiguationData":[OSD([subQ0])],"isStart":true})]});}
            fillet(context, id + "F16", {"entities" : qUnion([Q0, Q1, Q2, Q3, Q4, Q5, Q6, Q7, Q8, Q9, Q10, Q11, Q12, Q13]), "tangentPropagation" : true, "radius" : 5 * mm, "defaultsChanged" : false, "vertexSettings" : [], "allowEdgeOverflow" : false});
        }
    });
